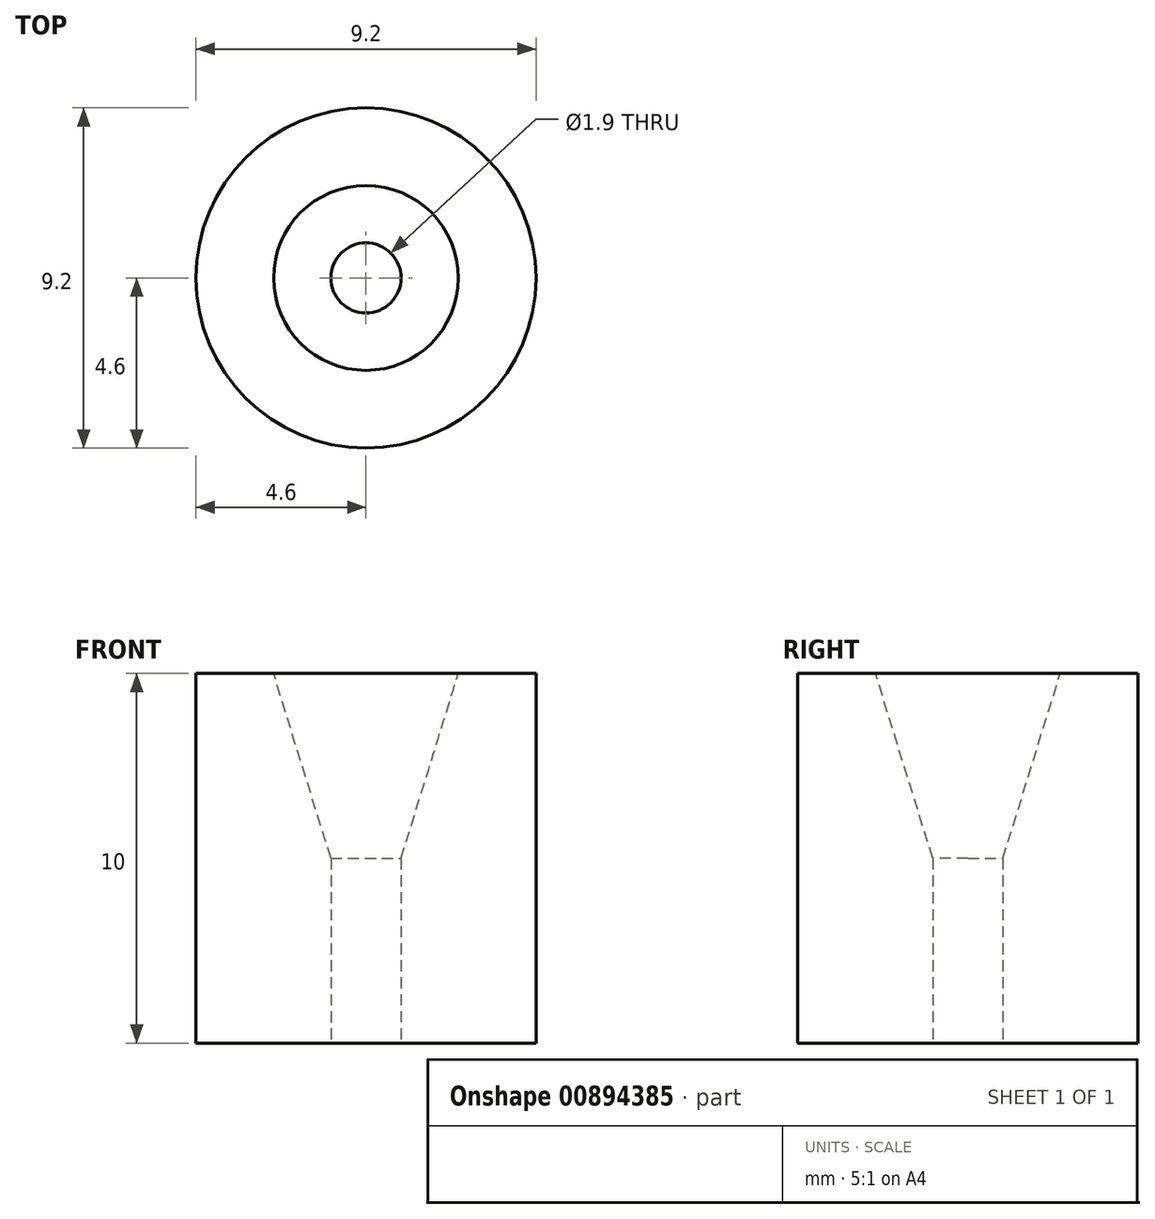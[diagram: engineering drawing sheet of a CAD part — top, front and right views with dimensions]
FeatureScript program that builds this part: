
annotation { "Feature Type Name" : "Feature", "Feature Type Description" : "" }
export const myFeature = defineFeature(function(context is Context, id is Id, definition is map)
    precondition{}
    {
        {
            var Q0;
            Q0=qCreatedBy(makeId("Top.planeOp"),FACE);
            var sketch = newSketch(context, id + "F0", { "sketchPlane" : qUnion([Q0])});
            skCircle(sketch, "E0", {"center": v(0, 0) * mm, "radius": 4.6 * mm});
            skSolve(sketch);
        }
        {
            var Q0;
            Q0=makeQuery(id+"F0.imprint","IMPRINT",FACE,{"disambiguationData":[TD([[makeQuery(id+"F0.imprint","IMPRINT",EDGE,{"derivedFrom":sQuery(id+"F0.wireOp",EDGE,"E0")}),1.0]])]});
            extrude(context, id + "F1", {"entities" : qUnion([Q0]), "depth" : 10 * mm, "offsetDistance" : 25 * mm});
        }
        {
            var Q0;
            Q0=makeQuery(id+"F1.opExtrude","CAP_FACE",FACE,{"disambiguationData":[OSD([sQuery(id+"F0.wireOp",EDGE,"E0")])],"isStart":true});
            var sketch = newSketch(context, id + "F2", { "sketchPlane" : qUnion([Q0])});
            skCircle(sketch, "E1", {"center": v(0, 0) * mm, "radius": 0.95 * mm});
            skSolve(sketch);
        }
        {
            var Q0;
            Q0=makeQuery(id+"F1.opExtrude","CAP_FACE",FACE,{"disambiguationData":[OSD([sQuery(id+"F0.wireOp",EDGE,"E0")])],"isStart":false});
            var sketch = newSketch(context, id + "F3", { "sketchPlane" : qUnion([Q0])});
            skCircle(sketch, "E2", {"center": v(0, 0) * mm, "radius": 2.5 * mm});
            skSolve(sketch);
        }
        {
            var Q0;
            Q0=makeQuery(id+"F2.imprint","IMPRINT",FACE,{"disambiguationData":[TD([[makeQuery(id+"F2.imprint","IMPRINT",EDGE,{"derivedFrom":sQuery(id+"F2.wireOp",EDGE,"E1")}),1.0]])]});
            var Q1;
            Q1=sQuery(id+"F2.wireOp",EDGE,"E1");
            extrude(context, id + "F4", {"entities" : qUnion([Q0]), "operationType" : NewBodyOperationType.REMOVE, "surfaceEntities" : qUnion([Q1]), "oppositeDirection" : true, "depth" : 5 * mm, "offsetDistance" : 25 * mm});
        }
        {
            var Q1;
            Q1=makeQuery(id+"F4.boolean.opBoolean","COPY",FACE,{"derivedFrom":makeQuery(id+"F4.opExtrude","CAP_FACE",FACE,{"disambiguationData":[OSD([sQuery(id+"F2.wireOp",EDGE,"E1")])],"isStart":false})});
            var Q2;
            Q2=makeQuery(id+"F3.imprint","IMPRINT",FACE,{"disambiguationData":[TD([[makeQuery(id+"F3.imprint","IMPRINT",EDGE,{"derivedFrom":sQuery(id+"F3.wireOp",EDGE,"E2")}),1.0]])]});
            loft(context, id + "F5", {"operationType" : NewBodyOperationType.REMOVE, "sheetProfilesArray" : [{ "sheetProfileEntities" : qUnion([Q1]) }, { "sheetProfileEntities" : qUnion([Q2]) }]});
        }
    });
